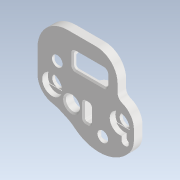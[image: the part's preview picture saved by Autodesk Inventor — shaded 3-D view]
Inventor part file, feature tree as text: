
AUTODESK INVENTOR PART (.ipt)
format: ipt  version: 2022.1 (Build 261234020, 234B)  size: 748,544 bytes
history: native  units: mm
features: reference x21, sketch x14, extrude x13, fillet x12, other x10, projected_geometry x9, delete_face x5, direct_edit x5, move_body x5, chamfer x4, hole x1
ambient origin geometry x8: Origin, YZ Plane, XZ Plane, XY Plane, X Axis, Y Axis, Z Axis, Center Point
bodies: Volumenkörper1 (feature_tree)
feature tree (99):
  extrude  "Extrusion1"  Depth=2.0mm
  delete_face  "Fläche löschen1"
  hole  "Bohrung1"  [1 undecoded]
  extrude  "Extrusion2"  Depth=1.0mm
  extrude  "Extrusion3"  Depth=0.8mm
  extrude  "Extrusion4"  Depth=1.0mm
  fillet  "Rundung1"  Radius=1.0mm
  fillet  "Rundung2"  Radius=1.0mm
  fillet  "Rundung3"  Radius=1.0mm
  delete_face  "Fläche löschen2"
  fillet  "Rundung4"  Radius=1.0mm
  fillet  "Rundung5"  Radius=1.0mm
  fillet  "Rundung6"  Radius=1.0mm
  fillet  "Rundung7"  Radius=1.0mm
  extrude  "Extrusion5"  Depth=1.0mm
  direct_edit  "Direktbearbeitung1"
  direct_edit  "Direktbearbeitung2"
  chamfer  "Fase2"  [1 undecoded]
  extrude  "Extrusion6"  Depth=10.0mm
  extrude  "Extrusion7"  TaperAngle=45.0deg  [1 undecoded]
  extrude  "Extrusion8"  Depth=10.0mm
  chamfer  "Fase3"  Distance=4.0mm
  fillet  "Rundung8"  Radius=5.0mm
  extrude  "Extrusion9"  Depth=10.0mm
  delete_face  "Fläche löschen3"
  extrude  "Extrusion10"  Depth=10.0mm
  extrude  "Extrusion11"  TaperAngle=0.0deg  [1 undecoded]
  direct_edit  "Direktbearbeitung3"
  direct_edit  "Direktbearbeitung4"
  delete_face  "Fläche löschen4"
  delete_face  "Fläche löschen5"
  chamfer  "Fase4"  Distance=2.4mm
  fillet  "Rundung9"  Radius=5.0mm
  fillet  "Rundung10"  Radius=2.0mm
  chamfer  "Fase5"  Distance=6.0mm
  extrude  "Extrusion12"  Depth=10.0mm
  fillet  "Rundung11"  Radius=5.0mm
  fillet  "Rundung12"  Radius=10.0mm
  direct_edit  "Direktbearbeitung5"
  extrude  "Extrusion13"  Depth=10.0mm
  sketch  "Skizze1"  dims[d0=2.0mm d1=0.0mm]
  reference  "Referenz1"
  reference  "Referenz2"
  reference  "Referenz3"
  reference  "Referenz4"
  reference  "Referenz5"
  reference  "Referenz6"
  reference  "Referenz7"
  reference  "Referenz8"
  reference  "Referenz9"
  reference  "Referenz10"
  reference  "Referenz11"
  reference  "Referenz12"
  sketch  "Skizze2"  dims[d2=3.0mm d3=6.0mm d4=4.0mm d5=2.0mm d6=90.0deg d7=8.0mm d8=20.594885mm d9=3.0mm]
  reference  "Referenz13"
  reference  "Referenz14"
  sketch  "Skizze3"  dims[d10=2.0mm d11=0.0mm d12=1.0mm]
  sketch  "Skizze4"  dims[d13=1.0mm d14=1.0mm]
  reference  "Referenz15"
  sketch  "Skizze5"  dims[d15=1.0mm d16=0.8mm]
  reference  "Referenz16"
  projected_geometry  "Projizierte Kontur1"
  sketch  "Skizze6"  dims[d17=1.0mm d18=1.0mm d19=1.0mm d20=1.0mm d21=1.0mm d22=1.0mm d23=1.0mm d24=1.0mm d25=1.0mm]
  sketch  "Skizze7"  dims[d26=1.0mm d27=1.0mm]
  sketch  "Skizze8"  dims[d28=1.0mm]
  projected_geometry  "Projizierte Kontur2"
  projected_geometry  "Projizierte Kontur3"
  sketch  "Skizze9"  dims[d29=1.0mm]
  reference  "Referenz17"
  reference  "Referenz18"
  sketch  "Skizze10"  dims[d30=1.0mm]
  reference  "Referenz19"
  reference  "Referenz20"
  reference  "Referenz21"
  sketch  "Skizze11"  dims[d31=1.0mm]
  projected_geometry  "Projizierte Kontur4"
  projected_geometry  "Projizierte Kontur5"
  sketch  "Skizze12"  dims[d32=1.0mm]
  projected_geometry  "Projizierte Kontur6"
  projected_geometry  "Projizierte Kontur7"
  sketch  "Skizze13"  dims[d33=0.6mm d34=0.0mm d35=0.0mm]
  projected_geometry  "Projizierte Kontur8"
  sketch  "Skizze15"  dims[d36=4.0mm d37=4.0mm d38=45.0deg d39=4.0mm d40=4.0mm d41=5.0mm d42=3.0mm d43=3.0mm d44=0.0mm d45=0.0mm d46=2.4mm d47=5.0mm d48=2.0mm d49=6.0mm d50=10.0mm d51=5.0mm d52=10.0mm d53=10.0mm d57=5.5mm d58=5.5mm d59=5.5mm d60=5.5mm d61=1.6mm d62=0.0mm d63=0.0mm d64=0.0mm d65=0.4mm d66=1.0mm d67=0.0mm d68=0.0mm d69=0.4mm d70=2.0mm d71=45.0deg d72=5.6mm d73=5.6mm d74=1.6mm d75=0.0mm d76=0.2mm d77=0.0mm d78=1.4mm d79=0.0mm d80=0.4mm d81=2.0mm d82=45.0deg d83=2.0mm d84=1.0mm d85=1.0mm d86=1.0mm d87=1.0mm d88=0.8mm d89=0.0mm d90=0.0mm d91=10.0mm d92=0.0mm d93=10.0mm d94=0.0mm d95=0.0mm d96=0.0mm d97=-0.2mm d98=0.0mm d99=-0.6mm d100=0.0mm d101=1.0mm d102=2.0mm d103=45.0deg d104=1.0mm d105=2.0mm d106=0.4mm d107=2.0mm d108=45.0deg d109=10.0mm d110=0.0mm d111=10.0mm d112=1.0mm d113=0.0mm d114=0.0mm d115=-0.5mm d116=10.0mm d117=0.0mm]
  projected_geometry  "Projizierte Kontur9"
  other  "<userpath>\Desktop\RAMA_SBNG\Toolhead_SBOnly.iam"
  other  "Toolhead_SBOnly.iam"
  other  "LGX_Lite_Stealthburner_Normal:1"
  other  "Front_body_LGX_Lite_Stealthburner_rev02"
  other  "2PC-SB-PCB:1"
  other  "Bauteil52"
  other  "LGX-Lite Dummy"
  other  "<userpath>\Desktop\RAMA_SBNG\Baugruppe268.iam"
  other  "Baugruppe268.iam"
  move_body  "Verschieben1"
  move_body  "Verschieben2"
  other  "LGX-Lite Dummy:1"
  move_body  "Verschieben3"
  move_body  "Verschieben4"
  move_body  "Verschieben5"
note: 4 required parameter values undecoded (feature->parameter linkage not recoverable at this tier; creation-order binding heuristic only, values carry confidence <= 0.55)
